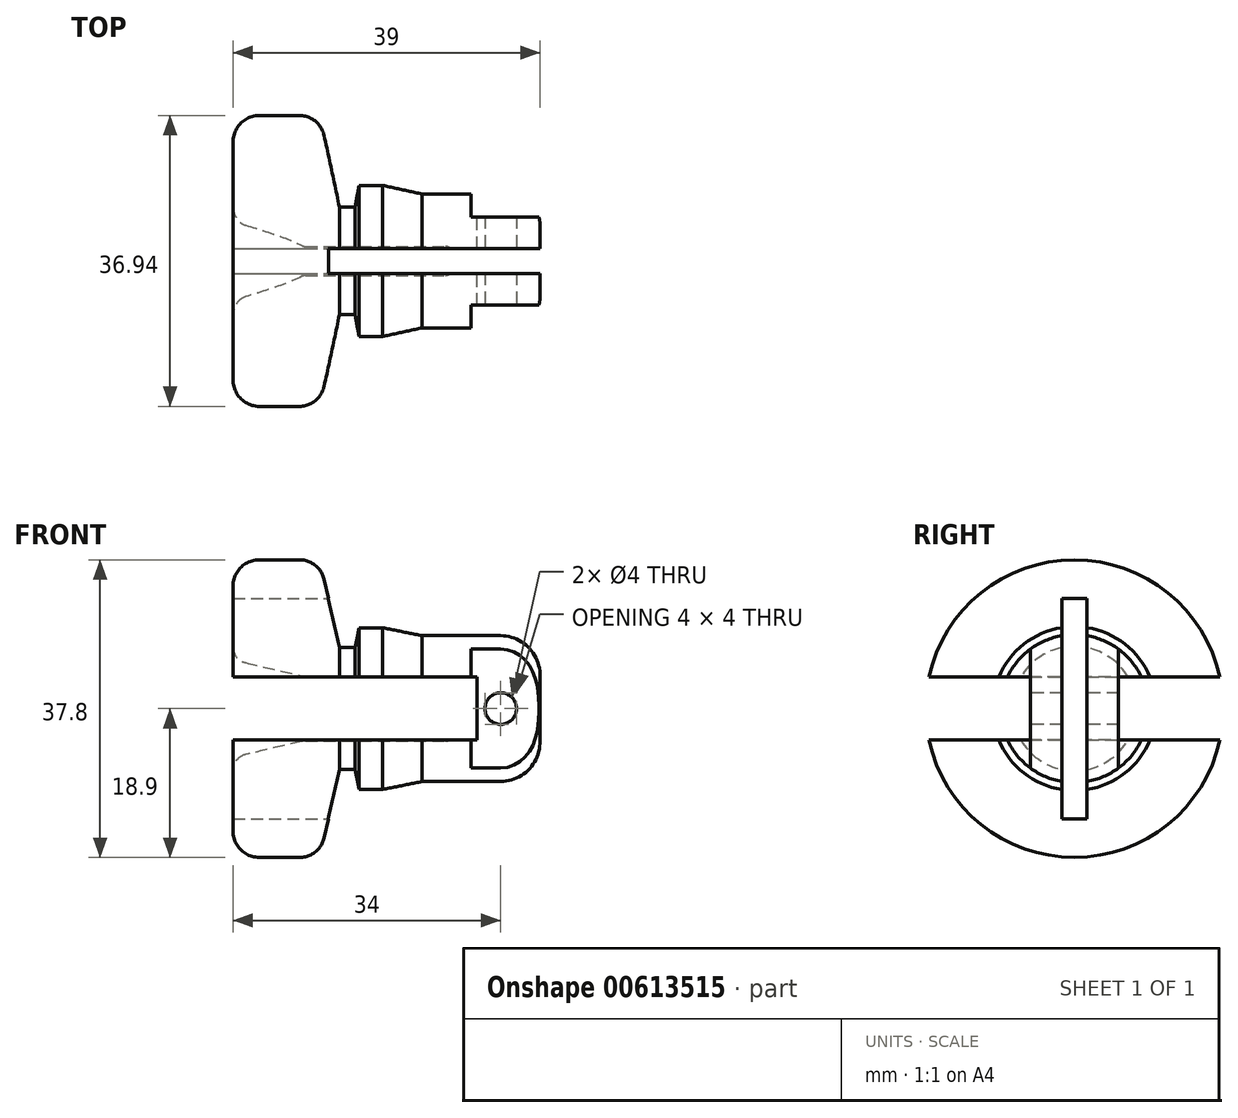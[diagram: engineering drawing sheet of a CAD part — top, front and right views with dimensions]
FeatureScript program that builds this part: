
annotation { "Feature Type Name" : "Feature", "Feature Type Description" : "" }
export const myFeature = defineFeature(function(context is Context, id is Id, definition is map)
    precondition{}
    {
        {
            var Q0;
            Q0=qCreatedBy(makeId("Front.planeOp"),FACE);
            var sketch = newSketch(context, id + "F0", { "sketchPlane" : qUnion([Q0])});
            skLineSegment(sketch, "E0", {"start": v(-20.5, 7.9) * mm, "end": v(-18.5, 7.9) * mm});
            skLineSegment(sketch, "E1", {"start": v(-18.5, 7.9) * mm, "end": v(-18, 10.4) * mm});
            skLineSegment(sketch, "E2", {"start": v(-18, 10.4) * mm, "end": v(-15, 10.4) * mm});
            skLineSegment(sketch, "E3", {"start": v(5, 4.4) * mm, "end": v(5, 0) * mm});
            skLineSegment(sketch, "E4", {"start": v(-20.5, 7.9) * mm, "end": v(-22.44, 16.42) * mm});
            skLineSegment(sketch, "E5", {"start": v(-25.54, 18.9) * mm, "end": v(-30.7, 18.9) * mm});
            skLineSegment(sketch, "E6", {"start": v(-34, 15.6) * mm, "end": v(-34, 8) * mm});
            skLineSegment(sketch, "E7", {"start": v(-15, 10.4) * mm, "end": v(-10, 9.4) * mm});
            skLineSegment(sketch, "E8", {"start": v(-10, 9.4) * mm, "end": v(0, 9.4) * mm});
            skLineSegment(sketch, "E9", {"start": v(-32.43, 6.05) * mm, "end": v(-25.21, 4.45) * mm});
            skLineSegment(sketch, "E10", {"start": v(-24.78, 4.4) * mm, "end": v(-7, 4.4) * mm});
            skLineSegment(sketch, "E11", {"start": v(-5, 2.4) * mm, "end": v(-5, 0) * mm});
            skArc(sketch, "E12", {"start": v(-30.7, 18.9) * mm, "mid": v(-33.03, 17.93) * mm, "end": v(-34, 15.6) * mm});
            skArc(sketch, "E13", {"start": v(-22.44, 16.42) * mm, "mid": v(-23.56, 18.2) * mm, "end": v(-25.54, 18.9) * mm});
            skPoint(sketch, "E14.orphan", {"position": v(-23, 18.9) * mm});
            skArc(sketch, "E15.filletArc", {"start": v(5, 4.4) * mm, "mid": v(3.54, 7.94) * mm, "end": v(0, 9.4) * mm});
            skPoint(sketch, "E16.visualSharp", {"position": v(-34, 6.4) * mm});
            skArc(sketch, "E16.filletArc", {"start": v(-34, 8) * mm, "mid": v(-33.56, 6.75) * mm, "end": v(-32.43, 6.05) * mm});
            skPoint(sketch, "E17.visualSharp", {"position": v(-5, 4.4) * mm});
            skArc(sketch, "E17.filletArc", {"start": v(-5, 2.4) * mm, "mid": v(-5.59, 3.81) * mm, "end": v(-7, 4.4) * mm});
            skPoint(sketch, "E18.visualSharp", {"position": v(-25, 4.4) * mm});
            skArc(sketch, "E18.filletArc", {"start": v(-25.21, 4.45) * mm, "mid": v(-25, 4.41) * mm, "end": v(-24.78, 4.4) * mm});
            skLineSegment(sketch, "E19", {"start": v(5, 0) * mm, "end": v(-5, 0) * mm});
            skSolve(sketch);
        }
        {
            var Q0;
            Q0=qSketchRegion(id+"F0",true);
            var Q1;
            Q1=sQuery(id+"F0.wireOp",EDGE,"E19");
            revolve(context, id + "F1", {"entities" : qUnion([Q0]), "axis" : qUnion([Q1]), "revolveType" : RevolveType.FULL});
        }
        {
            var Q0;
            Q0=qCreatedBy(makeId("Right.planeOp"),FACE);
            var sketch = newSketch(context, id + "F2", { "sketchPlane" : qUnion([Q0])});
            skLineSegment(sketch, "E20.bottom", {"start": v(-1.6, -14) * mm, "end": v(1.6, -14) * mm});
            skLineSegment(sketch, "E20.top", {"start": v(-1.6, 14) * mm, "end": v(1.6, 14) * mm});
            skLineSegment(sketch, "E20.left", {"start": v(-1.6, -14) * mm, "end": v(-1.6, 14) * mm});
            skLineSegment(sketch, "E20.right", {"start": v(1.6, -14) * mm, "end": v(1.6, 14) * mm});
            skPoint(sketch, "E20.middle", {"position": v(0, 0) * mm});
            skSolve(sketch);
        }
        {
            var Q0;
            Q0=qSketchRegion(id+"F2",true);
            extrude(context, id + "F3", {"entities" : qUnion([Q0]), "operationType" : NewBodyOperationType.REMOVE, "oppositeDirection" : true, "depth" : 100 * mm, "offsetDistance" : 25 * mm, "symmetric" : true});
        }
        {
            var Q0;
            Q0=qCreatedBy(makeId("Right.planeOp"),FACE);
            cPlane(context, id + "F4", {"entities" : qUnion([Q0]), "cplaneType" : CPlaneType.OFFSET, "offset" : 3 * mm, "oppositeDirection" : true, "width" : 150 * mm, "height" : 150 * mm});
        }
        {
            var Q0;
            Q0=qCreatedBy(id+"F4.planeOp",FACE);
            var sketch = newSketch(context, id + "F5", { "sketchPlane" : qUnion([Q0])});
            skLineSegment(sketch, "E21.bottom", {"start": v(-24.97, -4) * mm, "end": v(24.97, -4) * mm});
            skLineSegment(sketch, "E21.top", {"start": v(-24.97, 4) * mm, "end": v(24.97, 4) * mm});
            skLineSegment(sketch, "E21.left", {"start": v(-24.97, -4) * mm, "end": v(-24.97, 4) * mm});
            skLineSegment(sketch, "E21.right", {"start": v(24.97, -4) * mm, "end": v(24.97, 4) * mm});
            skPoint(sketch, "E21.middle", {"position": v(0, 0) * mm});
            skSolve(sketch);
        }
        {
            var Q0;
            Q0=qSketchRegion(id+"F5",true);
            extrude(context, id + "F6", {"entities" : qUnion([Q0]), "operationType" : NewBodyOperationType.REMOVE, "oppositeDirection" : true, "depth" : 32 * mm, "offsetDistance" : 25 * mm});
        }
        {
            var Q0;
            Q0=qCreatedBy(makeId("Front.planeOp"),FACE);
            var sketch = newSketch(context, id + "F7", { "sketchPlane" : qUnion([Q0])});
            skCircle(sketch, "E22", {"center": v(0, 0) * mm, "radius": 2 * mm});
            skSolve(sketch);
        }
        {
            var Q0;
            Q0=qSketchRegion(id+"F7",true);
            extrude(context, id + "F8", {"entities" : qUnion([Q0]), "operationType" : NewBodyOperationType.REMOVE, "oppositeDirection" : true, "depth" : 25 * mm, "offsetDistance" : 25 * mm, "symmetric" : true});
        }
        {
            var Q0;
            Q0=qCreatedBy(makeId("Top.planeOp"),FACE);
            var sketch = newSketch(context, id + "F9", { "sketchPlane" : qUnion([Q0])});
            skLineSegment(sketch, "E23", {"start": v(-3.8, 9.6) * mm, "end": v(-3.8, 5.6) * mm});
            skLineSegment(sketch, "E24", {"start": v(-3.8, 5.6) * mm, "end": v(5.7, 5.6) * mm});
            skLineSegment(sketch, "E25", {"start": v(5.7, 5.6) * mm, "end": v(5.7, 9.6) * mm});
            skLineSegment(sketch, "E26", {"start": v(5.7, 9.6) * mm, "end": v(-3.8, 9.6) * mm});
            skLineSegment(sketch, "E27.MirrorCS", {"start": v(5.7, -5.6) * mm, "end": v(5.7, -9.6) * mm});
            skLineSegment(sketch, "E28.MirrorCS", {"start": v(-3.8, -5.6) * mm, "end": v(5.7, -5.6) * mm});
            skLineSegment(sketch, "E29.MirrorCS", {"start": v(-3.8, -9.6) * mm, "end": v(-3.8, -5.6) * mm});
            skLineSegment(sketch, "E30.MirrorCS", {"start": v(5.7, -9.6) * mm, "end": v(-3.8, -9.6) * mm});
            skSolve(sketch);
        }
        {
            var Q0;
            Q0=qSketchRegion(id+"F9",true);
            extrude(context, id + "F10", {"entities" : qUnion([Q0]), "operationType" : NewBodyOperationType.REMOVE, "oppositeDirection" : true, "depth" : 25 * mm, "offsetDistance" : 25 * mm, "symmetric" : true});
        }
    });
